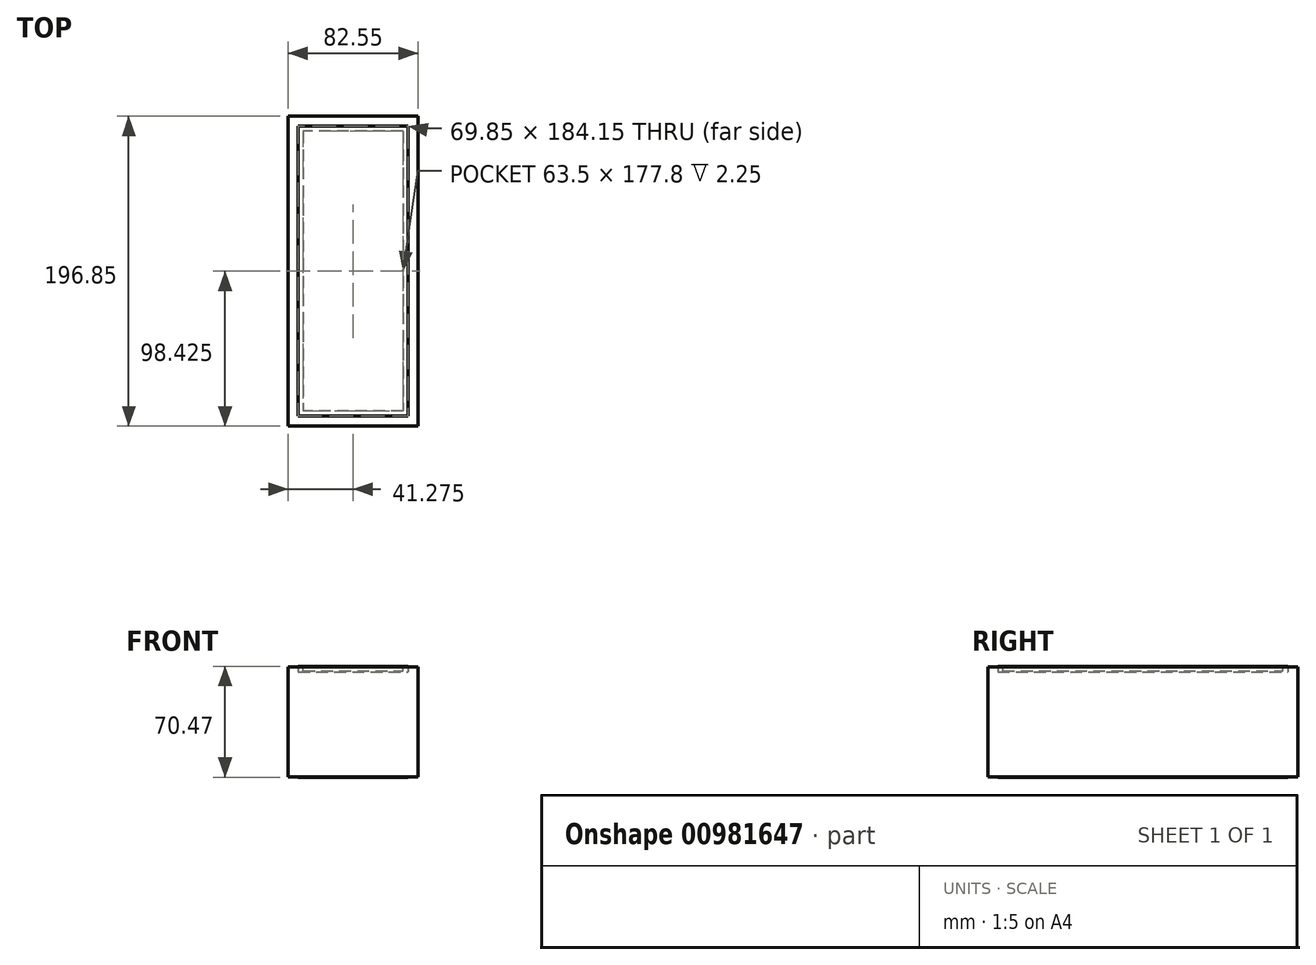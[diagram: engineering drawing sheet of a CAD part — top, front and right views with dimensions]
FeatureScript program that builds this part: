
annotation { "Feature Type Name" : "Feature", "Feature Type Description" : "" }
export const myFeature = defineFeature(function(context is Context, id is Id, definition is map)
    precondition{}
    {
        {
            assignVariable(context, id + "F0", {"name" : "height", "anyValue" : 2.75});
        }
        {
            assignVariable(context, id + "F1", {"name" : "OffsetA", "anyValue" : .25});
        }
        {
            assignVariable(context, id + "F2", {"name" : "OffsetB", "anyValue" : 3 / 8});
        }
        {
            var Q0;
            Q0=qCreatedBy(makeId("Front.planeOp"),FACE);
            var sketch = newSketch(context, id + "F3", { "sketchPlane" : qUnion([Q0])});
            skLineSegment(sketch, "E0.bottom", {"start": v(0, 69.85) * mm, "end": v(82.55, 69.85) * mm});
            skLineSegment(sketch, "E0.top", {"start": v(0, 0) * mm, "end": v(82.55, 0) * mm});
            skLineSegment(sketch, "E0.left", {"start": v(0, 69.85) * mm, "end": v(0, 0) * mm});
            skLineSegment(sketch, "E0.right", {"start": v(82.55, 69.85) * mm, "end": v(82.55, 0) * mm});
            skSolve(sketch);
        }
        {
            var Q0;
            Q0=makeQuery(id+"F3.imprint","IMPRINT",FACE,{"disambiguationData":[TD([[makeQuery(id+"F3.imprint","IMPRINT",EDGE,{"derivedFrom":sQuery(id+"F3.wireOp",EDGE,"E0.bottom")}),-1.0]])]});
            extrude(context, id + "F4", {"entities" : qUnion([Q0]), "oppositeDirection" : true, "depth" : 196.85 * mm, "offsetDistance" : 25.4 * mm});
        }
        {
            var Q0;
            Q0=makeQuery(id+"F4.opExtrude","SWEPT_FACE",FACE,{"disambiguationData":[OSD([sQuery(id+"F3.wireOp",EDGE,"E0.top")])]});
            var sketch = newSketch(context, id + "F5", { "sketchPlane" : qUnion([Q0])});
            skLineSegment(sketch, "E1.bottom", {"start": v(76.2, -6.35) * mm, "end": v(6.35, -6.35) * mm});
            skLineSegment(sketch, "E1.top", {"start": v(76.2, -190.5) * mm, "end": v(6.35, -190.5) * mm});
            skLineSegment(sketch, "E1.left", {"start": v(76.2, -6.35) * mm, "end": v(76.2, -190.5) * mm});
            skLineSegment(sketch, "E1.right", {"start": v(6.35, -6.35) * mm, "end": v(6.35, -190.5) * mm});
            skSolve(sketch);
        }
        {
            var Q0;
            Q0=makeQuery(id+"F5.imprint","IMPRINT",FACE,{"disambiguationData":[TD([[makeQuery(id+"F5.imprint","IMPRINT",EDGE,{"derivedFrom":sQuery(id+"F5.wireOp",EDGE,"E1.bottom")}),1.0]])]});
            extrude(context, id + "F6", {"entities" : qUnion([Q0]), "operationType" : NewBodyOperationType.ADD, "depth" : (getVariable(context, 'OffsetA')) * mm, "offsetDistance" : 25.4 * mm});
        }
        {
            var Q0;
            Q0=makeQuery(id+"F4.opExtrude","SWEPT_FACE",FACE,{"disambiguationData":[OSD([sQuery(id+"F3.wireOp",EDGE,"E0.bottom")])]});
            var sketch = newSketch(context, id + "F7", { "sketchPlane" : qUnion([Q0])});
            skLineSegment(sketch, "E2.bottom", {"start": v(6.35, 6.35) * mm, "end": v(76.2, 6.35) * mm});
            skLineSegment(sketch, "E2.top", {"start": v(6.35, 190.5) * mm, "end": v(76.2, 190.5) * mm});
            skLineSegment(sketch, "E2.left", {"start": v(6.35, 6.35) * mm, "end": v(6.35, 190.5) * mm});
            skLineSegment(sketch, "E2.right", {"start": v(76.2, 6.35) * mm, "end": v(76.2, 190.5) * mm});
            skSolve(sketch);
        }
        {
            var Q0;
            Q0=makeQuery(id+"F7.imprint","IMPRINT",FACE,{"disambiguationData":[TD([[makeQuery(id+"F7.imprint","IMPRINT",EDGE,{"derivedFrom":sQuery(id+"F7.wireOp",EDGE,"E2.bottom")}),-1.0]])]});
            var sketch = newSketch(context, id + "F8", { "sketchPlane" : qUnion([Q0])});
            skLineSegment(sketch, "E3.bottom", {"start": v(9.53, 9.52) * mm, "end": v(73.03, 9.53) * mm});
            skLineSegment(sketch, "E3.top", {"start": v(9.52, 187.33) * mm, "end": v(73.02, 187.33) * mm});
            skLineSegment(sketch, "E3.left", {"start": v(9.53, 9.53) * mm, "end": v(9.52, 187.33) * mm});
            skLineSegment(sketch, "E3.right", {"start": v(73.03, 9.53) * mm, "end": v(73.02, 187.33) * mm});
            skSolve(sketch);
        }
        {
            var Q0;
            Q0=makeQuery(id+"F8.imprint","IMPRINT",FACE,{"disambiguationData":[TD([[makeQuery(id+"F8.imprint","IMPRINT",EDGE,{"derivedFrom":sQuery(id+"F8.wireOp",EDGE,"E3.bottom")}),1.0]])]});
            extrude(context, id + "F9", {"entities" : qUnion([Q0]), "operationType" : NewBodyOperationType.REMOVE, "oppositeDirection" : true, "depth" : (getVariable(context, 'height') - getVariable(context, 'OffsetA')) * mm, "offsetDistance" : 25.4 * mm});
        }
        {
            var Q0;
            Q0=makeQuery(id+"F7.imprint","IMPRINT",FACE,{"disambiguationData":[TD([[makeQuery(id+"F7.imprint","IMPRINT",EDGE,{"derivedFrom":sQuery(id+"F7.wireOp",EDGE,"E2.bottom")}),1.0]])]});
            extrude(context, id + "F10", {"entities" : qUnion([Q0]), "operationType" : NewBodyOperationType.REMOVE, "oppositeDirection" : true, "depth" : (getVariable(context, 'OffsetA')) * mm, "offsetDistance" : 25.4 * mm});
        }
        {
            var Q0;
            Q0 = qSketchRegion(id + "F7", true);
            extrude(context, id + "F11", {"entities" : qUnion([Q0]), "depth" : (getVariable(context, 'OffsetA')) * mm, "offsetDistance" : 25.4 * mm, "hasSecondDirection" : true, "secondDirectionOppositeDirection" : true, "secondDirectionDepth" : (getVariable(context, 'OffsetA')) * mm});
        }
        {
            var Q0;
            Q0 = qSketchRegion(id + "F7", true);
            extrude(context, id + "F12", {"entities" : qUnion([Q0]), "depth" : (getVariable(context, 'OffsetB')) * mm, "offsetDistance" : 25.4 * mm, "hasSecondDirection" : true, "secondDirectionOppositeDirection" : true, "secondDirectionDepth" : 3.17 * mm});
        }
    });
